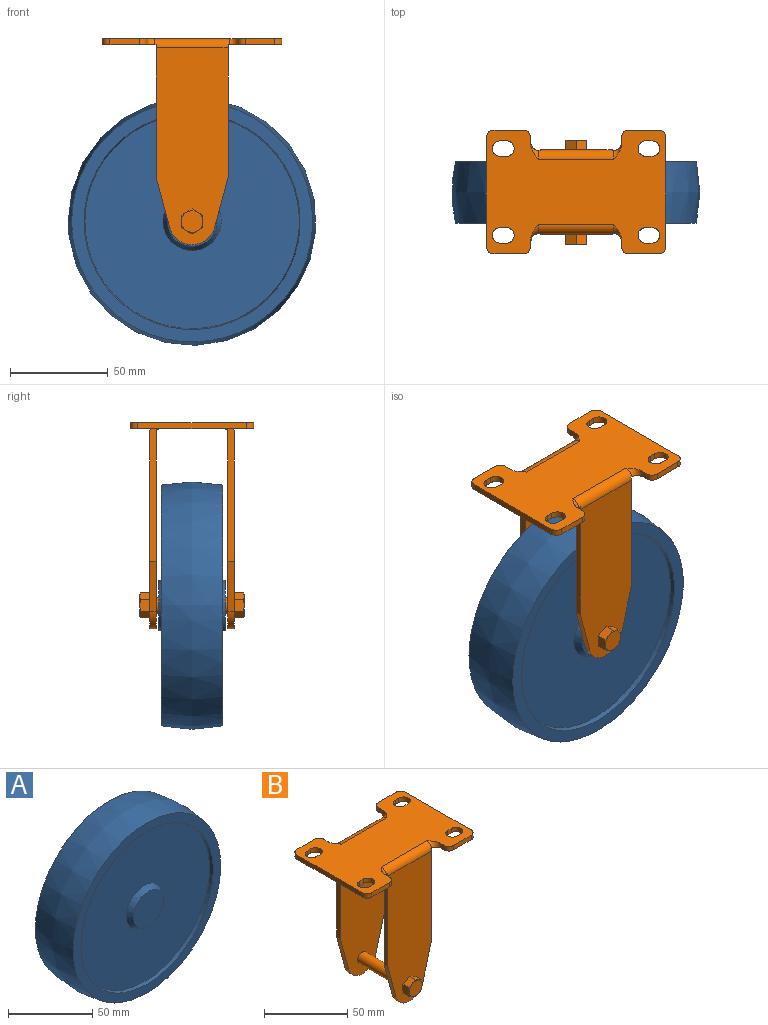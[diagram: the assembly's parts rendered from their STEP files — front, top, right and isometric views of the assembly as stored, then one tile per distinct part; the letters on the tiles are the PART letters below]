
ASSEMBLY  parts=2 mates=1
PART A: 11 faces, bbox 127x34.3x127 mm
  f0: cone r=12.7mm half-angle=30deg, axis (0,-1,0), area 381.5mm2, adj f9,f10
  f1: cone r=54.92mm half-angle=10deg, axis (0,1,0), area 893.7mm2, adj f8,f9
  f2: revolved ~127x127mm, area 12653.9mm2, adj f7,f8
  f3: cone r=55.37mm half-angle=10deg, axis (0,-1,0), area 893.7mm2, adj f6,f7
  f4: cone r=14.9mm half-angle=30deg, axis (0,1,0), area 381.5mm2, adj f5,f6
  f5: plane 25.4x25.4mm, normal (0,-1,0), area 506.7mm2, adj f4
  f6: plane 109.85x109.85mm, normal (0,-1,0), area 8779.7mm2, adj f3,f4
  f7: plane 123.44x123.44mm, normal (0,-1,0), area 2335.9mm2, adj f2,f3
  f8: plane 123.44x123.44mm, normal (0,1,0), area 2335.9mm2, adj f1,f2
  f9: plane 109.85x109.85mm, normal (0,1,0), area 8779.7mm2, adj f0,f1
  f10: plane 25.4x25.4mm, normal (0,1,0), area 506.7mm2, adj f0
PART B: 85 faces, bbox 93.5x65x114.8 mm
  f0: cylinder r=3.97mm len=36.83mm, axis (0,1,0), area 918.4mm2, adj f3,f4
  f1: plane 67.79x4.76mm, normal (-1,0,0), area 215.6mm2, adj f3,f7,f22,f45,f73,f75
  f2: plane 67.79x4.76mm, normal (1,0,0), area 215.6mm2, adj f3,f7,f26,f45,f73,f75
  f3: plane 100.81x36.83mm, normal (0,-1,0), area 3310.4mm2, adj f0,f1,f2,f22,f24,f26,f75
  f4: plane 100.81x36.83mm, normal (0,1,0), area 3310.4mm2, adj f0,f5,f6,f23,f25,f27,f76
  f5: plane 67.79x4.76mm, normal (-1,0,0), area 215.6mm2, adj f4,f21,f23,f45,f74,f76
  f6: plane 67.79x4.76mm, normal (1,0,0), area 215.6mm2, adj f4,f21,f27,f45,f74,f76
  f7: plane 100.81x36.83mm, normal (0,1,0), area 3253mm2, adj f1,f2,f22,f24,f26,f29,f30,f31
  f8: plane 6.08x5.68mm, normal (-0.5,0,-0.87), area 32mm2, adj f9,f13,f15,f16,f21
  f9: plane 6.08x5.68mm, normal (0.5,0,-0.87), area 32mm2, adj f8,f10,f14,f15,f21
  f10: plane 6.95x5.69mm, normal (1,0,0), area 32mm2, adj f9,f11,f14,f19,f21
  f11: plane 6.08x5.68mm, normal (0.5,0,0.87), area 32mm2, adj f10,f12,f18,f19,f21
  f12: plane 6.08x5.68mm, normal (-0.5,0,0.87), area 32mm2, adj f11,f13,f17,f18,f21
  f13: plane 6.95x5.69mm, normal (-1,0,0), area 32mm2, adj f8,f12,f16,f17,f21
  f14: cone r=5.56mm half-angle=60deg, axis (0,1,0), area 3mm2, adj f9,f10,f20
  f15: cone r=5.56mm half-angle=60deg, axis (0,1,0), area 3mm2, adj f8,f9,f20
  f16: cone r=5.56mm half-angle=60deg, axis (0,1,0), area 3mm2, adj f8,f13,f20
  f17: cone r=5.56mm half-angle=60deg, axis (0,1,0), area 3mm2, adj f12,f13,f20
  f18: cone r=5.56mm half-angle=60deg, axis (0,1,0), area 3mm2, adj f11,f12,f20
  f19: cone r=5.56mm half-angle=60deg, axis (0,1,0), area 3mm2, adj f10,f11,f20
  f20: plane 11.11x11.11mm, normal (0,-1,0), area 97mm2, adj f14,f15,f16,f17,f18,f19
  f21: plane 100.81x36.83mm, normal (0,-1,0), area 3253mm2, adj f5,f6,f8,f9,f10,f11,f12,f13
  f22: plane 25.78x6.91mm, normal (-0.97,0,-0.26), area 84.7mm2, adj f1,f3,f7,f24
  f23: plane 25.78x6.91mm, normal (-0.97,0,-0.26), area 84.7mm2, adj f4,f5,f21,f25
  f24: cylinder r=11.91mm len=23.01mm, axis (0,1,0), area 99mm2, adj f3,f7,f22,f26
  f25: cylinder r=11.91mm len=23.01mm, axis (0,1,0), area 99mm2, adj f4,f21,f23,f27
  f26: plane 25.78x6.91mm, normal (0.97,0,-0.26), area 84.7mm2, adj f2,f3,f7,f24
  f27: plane 25.78x6.91mm, normal (0.97,0,-0.26), area 84.7mm2, adj f4,f6,f21,f25
  f28: plane 93.53x64.95mm, normal (0,0,1), area 4176.7mm2, adj f42,f43,f44,f46,f47,f48,f49,f50
  f29: plane 6.08x5.68mm, normal (-0.5,0,-0.87), area 32mm2, adj f7,f30,f34,f36,f37
  f30: plane 6.08x5.68mm, normal (0.5,0,-0.87), area 32mm2, adj f7,f29,f31,f35,f36
  f31: plane 6.95x5.69mm, normal (1,0,0), area 32mm2, adj f7,f30,f32,f35,f40
  f32: plane 6.08x5.68mm, normal (0.5,0,0.87), area 32mm2, adj f7,f31,f33,f39,f40
  f33: plane 6.08x5.68mm, normal (-0.5,0,0.87), area 32mm2, adj f7,f32,f34,f38,f39
  f34: plane 6.95x5.69mm, normal (-1,0,0), area 32mm2, adj f7,f29,f33,f37,f38
  f35: cone r=5.56mm half-angle=60deg, axis (0,-1,0), area 3mm2, adj f30,f31,f41
  f36: cone r=5.56mm half-angle=60deg, axis (0,-1,0), area 3mm2, adj f29,f30,f41
  f37: cone r=5.56mm half-angle=60deg, axis (0,-1,0), area 3mm2, adj f29,f34,f41
  f38: cone r=5.56mm half-angle=60deg, axis (0,-1,0), area 3mm2, adj f33,f34,f41
  f39: cone r=5.56mm half-angle=60deg, axis (0,-1,0), area 3mm2, adj f32,f33,f41
  f40: cone r=5.56mm half-angle=60deg, axis (0,-1,0), area 3mm2, adj f31,f32,f41
  f41: plane 11.11x11.11mm, normal (0,1,0), area 97mm2, adj f35,f36,f37,f38,f39,f40
  f42: plane 14.94x3.18mm, normal (0,1,0), area 47.4mm2, adj f28,f45,f48,f83
  f43: plane 14.94x3.18mm, normal (0,-1,0), area 47.4mm2, adj f28,f45,f46,f84
  f44: plane 14.94x3.18mm, normal (0,-1,0), area 47.4mm2, adj f28,f45,f52,f82
  f45: plane 92.26x63.69mm, normal (0,0,-1), area 4237.2mm2, adj f1,f2,f5,f6,f42,f43,f44,f46
  f46: cylinder r=3.96mm len=3.96mm, axis (0,0,1), area 19.8mm2, adj f28,f43,f45,f47
  f47: plane 55.58x3.18mm, normal (-1,0,0), area 176.5mm2, adj f28,f45,f46,f48
  f48: cylinder r=3.96mm len=3.96mm, axis (0,0,1), area 19.8mm2, adj f28,f42,f45,f47
  f49: plane 14.94x3.18mm, normal (0,1,0), area 47.4mm2, adj f28,f45,f50,f81
  f50: cylinder r=3.96mm len=3.96mm, axis (0,0,1), area 19.8mm2, adj f28,f45,f49,f51
  f51: plane 55.58x3.18mm, normal (1,0,0), area 176.5mm2, adj f28,f45,f50,f52
  f52: cylinder r=3.96mm len=3.96mm, axis (0,0,1), area 19.8mm2, adj f28,f44,f45,f51
  f53: cylinder r=3.97mm len=7.94mm, axis (0,0,1), area 39.6mm2, adj f28,f45,f54,f56
  f54: plane 3.18x3.18mm, normal (0,-1,0), area 10.1mm2, adj f28,f45,f53,f55
  f55: cylinder r=3.97mm len=7.94mm, axis (0,0,1), area 39.6mm2, adj f28,f45,f54,f56
  f56: plane 3.18x3.18mm, normal (0,1,0), area 10.1mm2, adj f28,f45,f53,f55
  f57: cylinder r=3.97mm len=7.94mm, axis (0,0,1), area 39.6mm2, adj f28,f45,f58,f60
  f58: plane 3.18x3.18mm, normal (0,-1,0), area 10.1mm2, adj f28,f45,f57,f59
  f59: cylinder r=3.97mm len=7.94mm, axis (0,0,1), area 39.6mm2, adj f28,f45,f58,f60
  f60: plane 3.18x3.18mm, normal (0,1,0), area 10.1mm2, adj f28,f45,f57,f59
  f61: cylinder r=3.97mm len=7.94mm, axis (0,0,1), area 39.6mm2, adj f28,f45,f62,f64
  f62: plane 3.18x3.18mm, normal (0,-1,0), area 10.1mm2, adj f28,f45,f61,f63
  f63: cylinder r=3.97mm len=7.94mm, axis (0,0,1), area 39.6mm2, adj f28,f45,f62,f64
  f64: plane 3.18x3.18mm, normal (0,1,0), area 10.1mm2, adj f28,f45,f61,f63
  f65: cylinder r=3.97mm len=7.94mm, axis (0,0,1), area 39.6mm2, adj f28,f45,f66,f68
  f66: plane 3.18x3.18mm, normal (0,1,0), area 10.1mm2, adj f28,f45,f65,f67
  f67: cylinder r=3.97mm len=7.94mm, axis (0,0,1), area 39.6mm2, adj f28,f45,f66,f68
  f68: plane 3.18x3.18mm, normal (0,-1,0), area 10.1mm2, adj f28,f45,f65,f67
  f69: plane 3.65x3.18mm, normal (1,0,0), area 9.2mm2, adj f28,f45,f80,f84
  f70: plane 3.65x3.18mm, normal (-1,0,0), area 9.2mm2, adj f28,f45,f79,f82
  f71: plane 3.65x3.18mm, normal (1,0,0), area 9.2mm2, adj f28,f45,f77,f83
  f72: plane 3.65x3.18mm, normal (-1,0,0), area 9.2mm2, adj f28,f45,f78,f81
  f73: cylinder r=4.76mm len=38.43mm, axis (-1,0,0), area 284.9mm2, adj f1,f2,f7,f28,f45,f77,f78
  f74: cylinder r=4.76mm len=38.43mm, axis (1,0,0), area 284.9mm2, adj f5,f6,f21,f28,f45,f79,f80
  f75: cylinder r=1.59mm len=36.83mm, axis (-1,0,0), area 91.8mm2, adj f1,f2,f3,f45
  f76: cylinder r=1.59mm len=36.83mm, axis (1,0,0), area 91.8mm2, adj f4,f5,f6,f45
  f77: torus R=8.72mm, axis (-1,0,0), area 29.6mm2, adj f28,f45,f71,f73
  f78: torus R=8.72mm, axis (1,0,0), area 29.6mm2, adj f28,f45,f72,f73
  f79: torus R=8.72mm, axis (-1,0,0), area 29.6mm2, adj f28,f45,f70,f74
  f80: torus R=8.72mm, axis (1,0,0), area 29.6mm2, adj f28,f45,f69,f74
  f81: cylinder r=3.96mm len=3.96mm, axis (0,0,-1), area 19.8mm2, adj f28,f45,f49,f72
  f82: cylinder r=3.96mm len=3.96mm, axis (0,0,1), area 19.8mm2, adj f28,f44,f45,f70
  f83: cylinder r=3.96mm len=3.96mm, axis (0,0,1), area 19.8mm2, adj f28,f42,f45,f71
  f84: cylinder r=3.96mm len=3.96mm, axis (0,0,-1), area 19.8mm2, adj f28,f43,f45,f69
PLACE A t=(-8.82,-81.86,0.27)mm
PLACE B t=(-8.82,-81.86,0.27)mm
MATE revolute B.f0 <-> A.f0  axis (0,1,0) through (-8.82,-100.28,-93.4)mm
